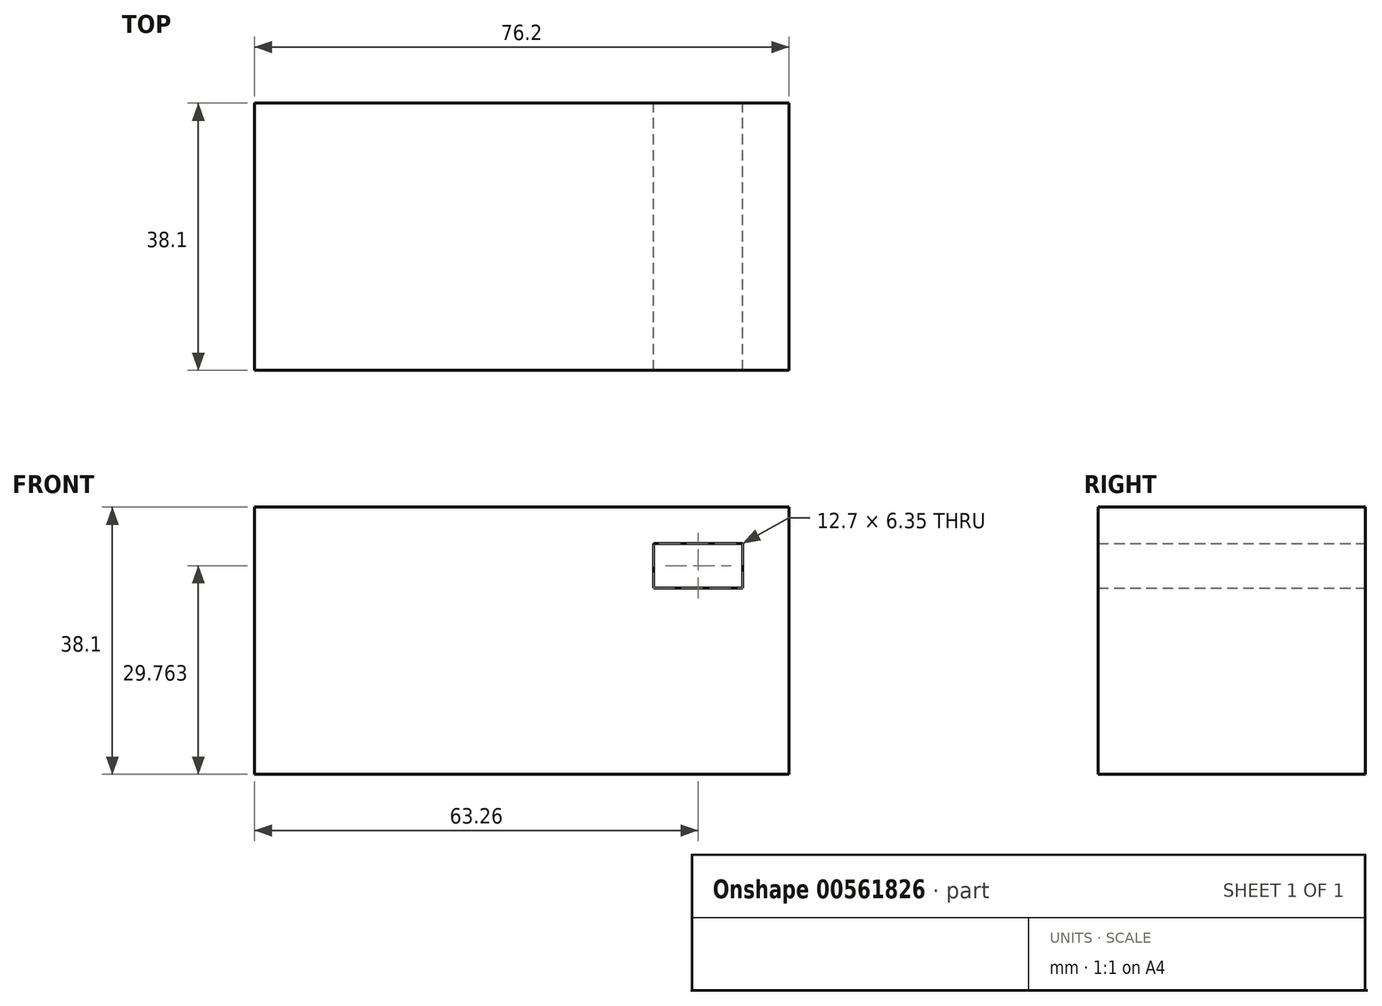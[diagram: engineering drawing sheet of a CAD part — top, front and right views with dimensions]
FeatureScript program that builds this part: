
annotation { "Feature Type Name" : "Feature", "Feature Type Description" : "" }
export const myFeature = defineFeature(function(context is Context, id is Id, definition is map)
    precondition{}
    {
        {
            var Q0;
            Q0=qCreatedBy(makeId("Front.planeOp"),FACE);
            var sketch = newSketch(context, id + "F0", { "sketchPlane" : qUnion([Q0])});
            skLineSegment(sketch, "E0.bottom", {"start": v(6.6, -13.39) * mm, "end": v(-69.6, -13.39) * mm});
            skLineSegment(sketch, "E0.top", {"start": v(6.6, 24.71) * mm, "end": v(-69.6, 24.71) * mm});
            skLineSegment(sketch, "E0.left", {"start": v(6.6, -13.39) * mm, "end": v(6.6, 24.71) * mm});
            skLineSegment(sketch, "E0.right", {"start": v(-69.6, -13.39) * mm, "end": v(-69.6, 24.71) * mm});
            skPoint(sketch, "E0.middle", {"position": v(-31.5, 5.66) * mm});
            skLineSegment(sketch, "E1.bottom", {"start": v(0, 13.2) * mm, "end": v(-12.7, 13.2) * mm});
            skLineSegment(sketch, "E1.top", {"start": v(0, 19.55) * mm, "end": v(-12.7, 19.55) * mm});
            skLineSegment(sketch, "E1.left", {"start": v(0, 13.2) * mm, "end": v(0, 19.55) * mm});
            skLineSegment(sketch, "E1.right", {"start": v(-12.7, 13.2) * mm, "end": v(-12.7, 19.55) * mm});
            skPoint(sketch, "E1.middle", {"position": v(-6.35, 16.37) * mm});
            skSolve(sketch);
        }
        {
            var Q0;
            Q0=makeQuery(id+"F0.imprint","IMPRINT",FACE,{"disambiguationData":[TD([[makeQuery(id+"F0.imprint","IMPRINT",EDGE,{"derivedFrom":sQuery(id+"F0.wireOp",EDGE,"E0.bottom")}),-1.0]])]});
            extrude(context, id + "F1", {"entities" : qUnion([Q0]), "depth" : 38.1 * mm, "offsetDistance" : 25.4 * mm});
        }
    });
